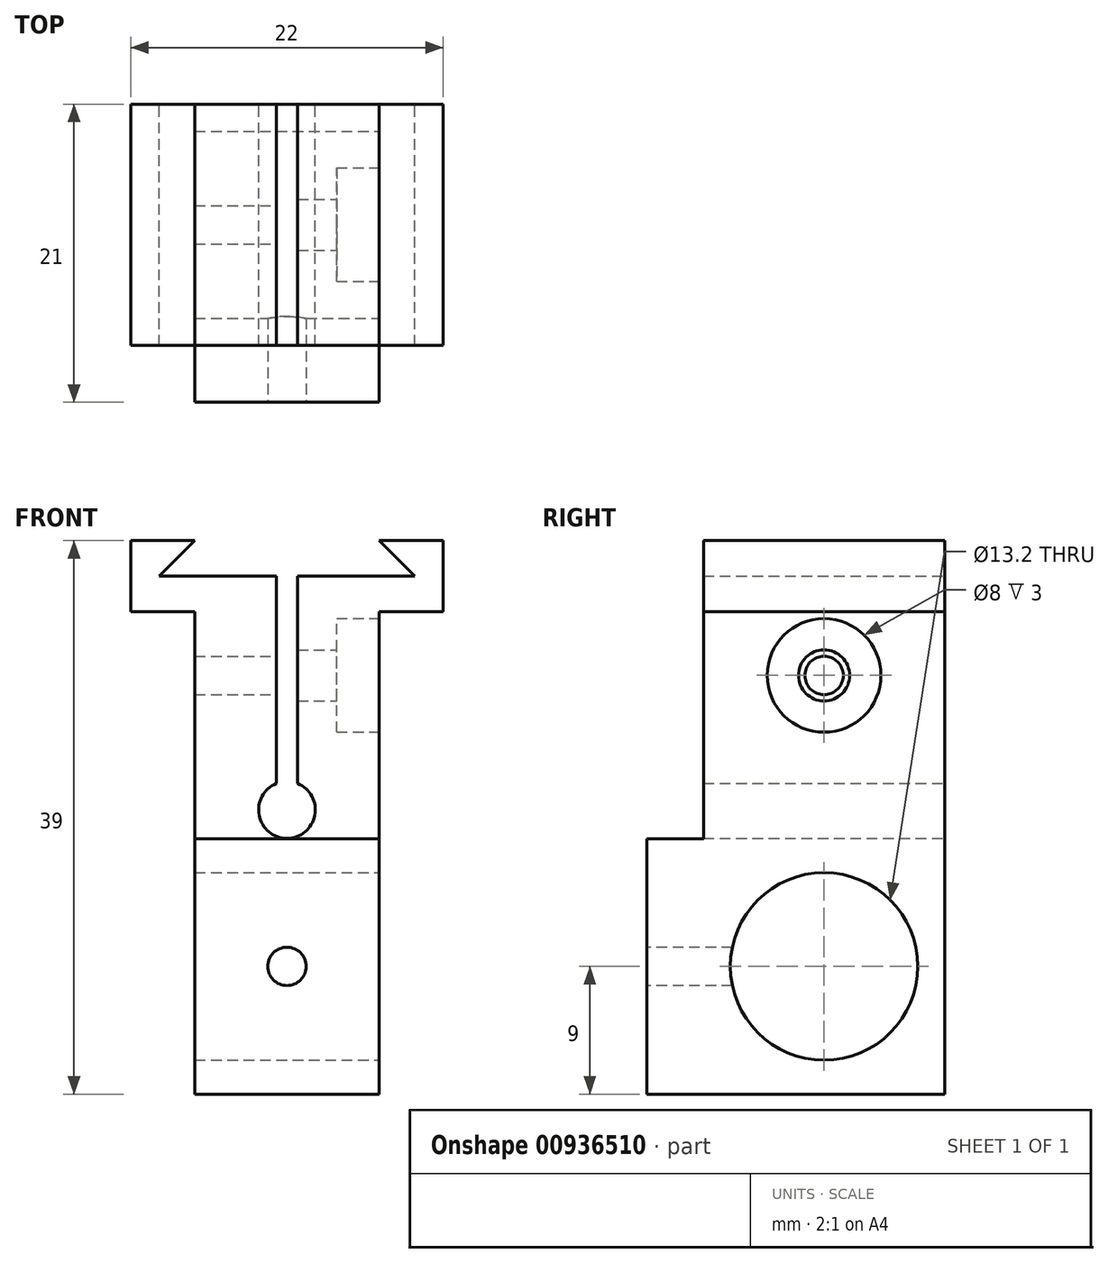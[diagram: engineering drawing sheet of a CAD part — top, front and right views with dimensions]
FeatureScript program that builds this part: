
annotation { "Feature Type Name" : "Feature", "Feature Type Description" : "" }
export const myFeature = defineFeature(function(context is Context, id is Id, definition is map)
    precondition{}
    {
        {
            var Q0;
            Q0=qCreatedBy(makeId("Front.planeOp"),FACE);
            var sketch = newSketch(context, id + "F0", { "sketchPlane" : qUnion([Q0])});
            skLineSegment(sketch, "E0", {"start": v(-6.5, 0) * mm, "end": v(-6.5, 0) * mm});
            skLineSegment(sketch, "E1", {"start": v(-6.5, 0) * mm, "end": v(-9, -2.5) * mm});
            skLineSegment(sketch, "E2", {"start": v(-9, -2.5) * mm, "end": v(-0.75, -2.5) * mm});
            skLineSegment(sketch, "E3", {"start": v(9, -2.5) * mm, "end": v(6.5, 0) * mm});
            skLineSegment(sketch, "E4", {"start": v(6.5, 0) * mm, "end": v(6.5, 0) * mm});
            skLineSegment(sketch, "E5", {"start": v(6.5, -5) * mm, "end": v(6.5, -39) * mm});
            skLineSegment(sketch, "E6", {"start": v(6.5, -39) * mm, "end": v(-6.5, -39) * mm});
            skLineSegment(sketch, "E7", {"start": v(-6.5, -39) * mm, "end": v(-6.5, -5) * mm});
            skLineSegment(sketch, "E8.left", {"start": v(-0.75, -2.5) * mm, "end": v(-0.75, -17.12) * mm});
            skLineSegment(sketch, "E8.right", {"start": v(0.75, -2.5) * mm, "end": v(0.75, -17.12) * mm});
            skArc(sketch, "E9", {"start": v(-0.75, -17.12) * mm, "mid": v(0, -20.97) * mm, "end": v(0.75, -17.12) * mm});
            skLineSegment(sketch, "E10", {"start": v(-21.05, -23) * mm, "end": v(19.49, -23) * mm, "construction": true});
            skPoint(sketch, "E11", {"position": v(0, -19.7) * mm});
            skPoint(sketch, "E12.orphan", {"position": v(0.75, -19.7) * mm});
            skPoint(sketch, "E8.top.start.orphan", {"position": v(-0.75, -19.7) * mm});
            skLineSegment(sketch, "E13.trimOffspring", {"start": v(0.75, -2.5) * mm, "end": v(9, -2.5) * mm});
            skPoint(sketch, "E8.bottom.start.orphan", {"position": v(-0.75, -1.35) * mm});
            skPoint(sketch, "E14.orphan", {"position": v(0.75, -1.35) * mm});
            skLineSegment(sketch, "E15", {"start": v(-6.5, -5) * mm, "end": v(-11, -5) * mm});
            skLineSegment(sketch, "E16", {"start": v(-11, -5) * mm, "end": v(-11, 0) * mm});
            skLineSegment(sketch, "E17", {"start": v(-11, 0) * mm, "end": v(-6.5, 0) * mm});
            skLineSegment(sketch, "E18", {"start": v(6.5, -5) * mm, "end": v(11, -5) * mm});
            skLineSegment(sketch, "E19", {"start": v(11, -5) * mm, "end": v(11, 0) * mm});
            skLineSegment(sketch, "E20", {"start": v(11, 0) * mm, "end": v(6.5, 0) * mm});
            skSolve(sketch);
        }
        {
            var Q0;
            Q0=makeQuery(id+"F0.imprint","IMPRINT",FACE,{"disambiguationData":[TD([[makeQuery(id+"F0.imprint","IMPRINT",EDGE,{"derivedFrom":sQuery(id+"F0.wireOp",EDGE,"E0")}),-1.0]])]});
            var Q1;
            Q1 = qSketchRegion(id + "F0", true);
            extrude(context, id + "F1", {"entities" : qUnion([Q0, Q1]), "depth" : 21 * mm, "offsetDistance" : 25 * mm});
        }
        {
            var Q0;
            Q0=makeQuery(id+"F1.opExtrude","CAP_FACE",FACE,{"disambiguationData":[OSD([sQuery(id+"F0.wireOp",EDGE,"E0"),sQuery(id+"F0.wireOp",EDGE,"E1"),sQuery(id+"F0.wireOp",EDGE,"E2"),sQuery(id+"F0.wireOp",EDGE,"E3"),sQuery(id+"F0.wireOp",EDGE,"E4"),sQuery(id+"F0.wireOp",EDGE,"E5"),sQuery(id+"F0.wireOp",EDGE,"E6"),sQuery(id+"F0.wireOp",EDGE,"E7"),sQuery(id+"F0.wireOp",EDGE,"E8.left"),sQuery(id+"F0.wireOp",EDGE,"E8.right"),sQuery(id+"F0.wireOp",EDGE,"E9"),sQuery(id+"F0.wireOp",EDGE,"E13.trimOffspring")])],"isStart":false});
            var sketch = newSketch(context, id + "F2", { "sketchPlane" : qUnion([Q0])});
            skLineSegment(sketch, "E21.top", {"start": v(-11, -21) * mm, "end": v(11, -21) * mm});
            skLineSegment(sketch, "E21.left", {"start": v(-11, 0) * mm, "end": v(-11, -21) * mm});
            skLineSegment(sketch, "E21.right", {"start": v(11, 0) * mm, "end": v(11, -21) * mm});
            skLineSegment(sketch, "E22", {"start": v(-11, 0) * mm, "end": v(11, 0) * mm});
            skSolve(sketch);
        }
        {
            var Q0;
            Q0 = qSketchRegion(id + "F2", true);
            extrude(context, id + "F3", {"entities" : qUnion([Q0]), "operationType" : NewBodyOperationType.REMOVE, "oppositeDirection" : true, "depth" : 4 * mm, "offsetDistance" : 25 * mm});
        }
        {
            var Q0;
            Q0=makeQuery(id+"F1.opExtrude","SWEPT_FACE",FACE,{"disambiguationData":[OSD([sQuery(id+"F0.wireOp",EDGE,"E5")])]});
            var sketch = newSketch(context, id + "F4", { "sketchPlane" : qUnion([Q0])});
            skLineSegment(sketch, "E23", {"start": v(-8.5, 1.16) * mm, "end": v(-8.5, -40.74) * mm, "construction": true});
            skPoint(sketch, "E23.startSnap0", {"position": v(-8.5, 0) * mm});
            skCircle(sketch, "E24", {"center": v(-8.5, -30) * mm, "radius": 6.6 * mm});
            skCircle(sketch, "E25", {"center": v(-8.5, -9.5) * mm, "radius": 1.35 * mm});
            skSolve(sketch);
        }
        {
            var Q0;
            Q0 = qSketchRegion(id + "F4", true);
            extrude(context, id + "F5", {"entities" : qUnion([Q0]), "operationType" : NewBodyOperationType.REMOVE, "endBound" : BoundingType.THROUGH_ALL, "oppositeDirection" : true, "depth" : 25 * mm, "offsetDistance" : 25 * mm});
        }
        {
            var Q0;
            Q0=makeQuery(id+"F1.opExtrude","SWEPT_FACE",FACE,{"disambiguationData":[OSD([sQuery(id+"F0.wireOp",EDGE,"E5")])]});
            var sketch = newSketch(context, id + "F6", { "sketchPlane" : qUnion([Q0])});
            skCircle(sketch, "E26", {"center": v(-8.5, -9.5) * mm, "radius": 1.8 * mm});
            skSolve(sketch);
        }
        {
            var Q0;
            Q0 = qSketchRegion(id + "F6", true);
            extrude(context, id + "F7", {"entities" : qUnion([Q0]), "operationType" : NewBodyOperationType.REMOVE, "oppositeDirection" : true, "depth" : 7 * mm, "offsetDistance" : 25 * mm});
        }
        {
            var Q0;
            Q0=makeQuery(id+"F1.opExtrude","SWEPT_FACE",FACE,{"disambiguationData":[OSD([sQuery(id+"F0.wireOp",EDGE,"E5")])]});
            var sketch = newSketch(context, id + "F8", { "sketchPlane" : qUnion([Q0])});
            skCircle(sketch, "E27", {"center": v(-8.5, -9.5) * mm, "radius": 4 * mm});
            skSolve(sketch);
        }
        {
            var Q0;
            Q0 = qSketchRegion(id + "F8", true);
            extrude(context, id + "F9", {"entities" : qUnion([Q0]), "operationType" : NewBodyOperationType.REMOVE, "oppositeDirection" : true, "depth" : 3 * mm, "offsetDistance" : 25 * mm});
        }
        {
            var Q0;
            Q0=makeQuery(id+"F1.opExtrude","CAP_FACE",FACE,{"disambiguationData":[OSD([sQuery(id+"F0.wireOp",EDGE,"E0"),sQuery(id+"F0.wireOp",EDGE,"E1"),sQuery(id+"F0.wireOp",EDGE,"E2"),sQuery(id+"F0.wireOp",EDGE,"E3"),sQuery(id+"F0.wireOp",EDGE,"E4"),sQuery(id+"F0.wireOp",EDGE,"E5"),sQuery(id+"F0.wireOp",EDGE,"E6"),sQuery(id+"F0.wireOp",EDGE,"E7"),sQuery(id+"F0.wireOp",EDGE,"E8.left"),sQuery(id+"F0.wireOp",EDGE,"E8.right"),sQuery(id+"F0.wireOp",EDGE,"E9"),sQuery(id+"F0.wireOp",EDGE,"E13.trimOffspring")])],"isStart":false});
            var sketch = newSketch(context, id + "F10", { "sketchPlane" : qUnion([Q0])});
            skLineSegment(sketch, "E28", {"start": v(14.64, -30) * mm, "end": v(-12.1, -30) * mm, "construction": true});
            skCircle(sketch, "E29", {"center": v(0, -30) * mm, "radius": 1.35 * mm});
            skSolve(sketch);
        }
        {
            var Q0;
            Q0 = qSketchRegion(id + "F10", true);
            extrude(context, id + "F11", {"entities" : qUnion([Q0]), "operationType" : NewBodyOperationType.REMOVE, "oppositeDirection" : true, "depth" : 12 * mm, "offsetDistance" : 25 * mm});
        }
    });
